# Revit family: Domotics-SerieCivili-GEWISS-27COMBI_SYSTEM-IP40_4P+4P+4P+4P_ORIZ
name_source: partatom
category: Apparecchi elettrici
revit_build: Autodesk Revit 2016 (Build: 20161004_0715(x64)
units: mm (PartAtom-declared; Revit-internal decimal feet)

## family parameters
Condiviso = No
Host = Superficie
Mantenere orientamento annotazione = No
Numero OmniClass = 23.80.30.14.24
Punto di calcolo locali = No
Quota connettore circolare = Usa diametro
Taglio con vuoti quando caricato = Sì
Tipo di parte = Normale
Titolo OmniClass = Junction Boxes

## types (1)
- Domotics-SerieCivili-GEWISS-27COMBI_SYSTEM-IP40_4P+4P+4P+4P_ORIZ
    Bidimensionale = bidimensionale system contenitori IP40 4X4P H : 4P
    Caratteristiche = Halogen free
    Catalogo = DOMOTICS
    Catalogo Serie = 27COMBI
    Classe isolamento = II
    Codice EAN = 8011564055315
    Codice Electrocod = 0212
    Colore = Grigio RAL 7035
    Configurazione = Modulo 4 x 4
    Coppia serraggio viti = 0,8NM
    Descrizione = CONTENITORE 16(4X4) POSTI ORIZZ.PROT.
    Descrizione: = 16 posti
    Dim. esterne BxHxP (mm) = 429x82x55
    Dimensioni BxHxP (mm) = 429x82x55
    Glow Wire Test = 650°C
    Grado di protezione = IP40
    IDF = 0c45c5e7-1e15-4c8d-8521-8a21acca27ae
    IDT = c435a9cb-b203-4528-9b1e-390a89cf94f5
    Immagine tipo = GW27008.jpg
    Larghezza scatola = 429 mm  [stored 1.40748 ft]
    Modello = GW27008
    N. fori Ã˜ 23 sfondabili = 18
    N. fori Ã˜ 23 sfondabili: = Laterali 18 / Sul fondo 4
    Norma di riferimento: = EN 60670-1
    Predisposizione scomparti = 2
    Produttore = GEWISS S.p.A.
    Prospetto di default = 1219 mm
    Resistenza agli urti = IK07
    SCATOLA = GEWISS GRIGIO
    SEO = Contenitore
    Scheda Tecnica = https://www.gewiss.com
    Temperatura di installazione = -25 +60 °C
    Termopressione con biglia = 70 °C
    Tipo sfondabili = Asportabili con utensile
    URL = https://www.gewiss.com
    Versione file RFA = 19.4
    Viti coperchio = Acciaio resistente alla corrosione

note: [stored X ft] marks values corroborated as IEEE doubles in the binary element streams (Revit-internal decimal feet)

## geometry (parser evidence)
native form markers: Blend x2
no freeform markers — native parametric forms only
